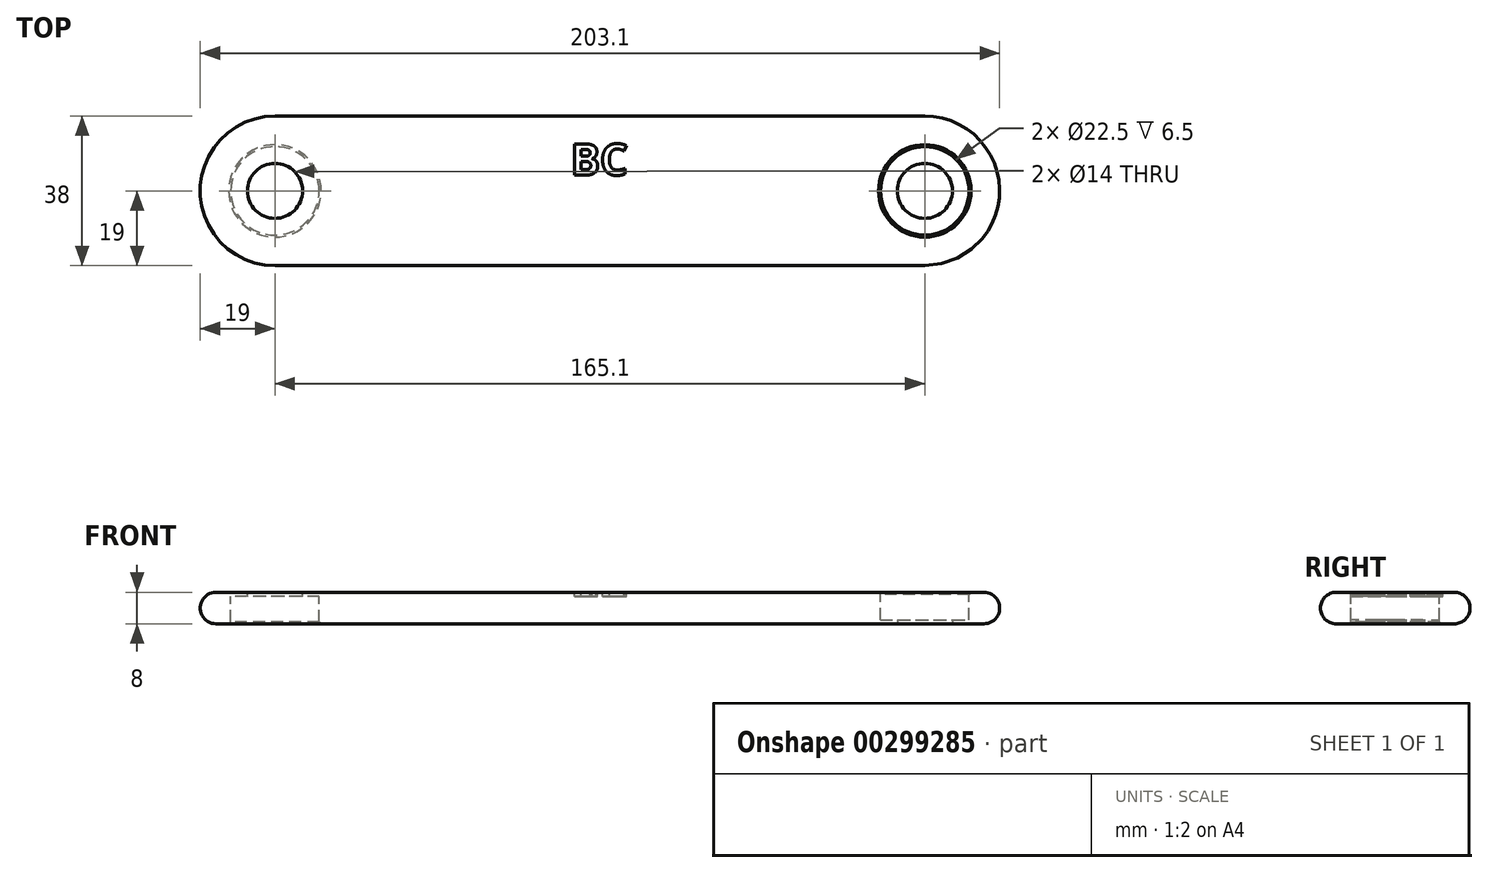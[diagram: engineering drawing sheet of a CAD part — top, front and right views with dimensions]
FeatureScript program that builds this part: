
annotation { "Feature Type Name" : "Feature", "Feature Type Description" : "" }
export const myFeature = defineFeature(function(context is Context, id is Id, definition is map)
    precondition{}
    {
        {
            var Q0;
            Q0=qCreatedBy(makeId("Top.planeOp"),FACE);
            var sketch = newSketch(context, id + "F0", { "sketchPlane" : qUnion([Q0])});
            skArc(sketch, "E0", {"start": v(-82.55, 19) * mm, "mid": v(-101.55, 0) * mm, "end": v(-82.55, -19) * mm});
            skArc(sketch, "E1", {"start": v(82.55, -19) * mm, "mid": v(101.55, 0) * mm, "end": v(82.55, 19) * mm});
            skCircle(sketch, "E2", {"center": v(-82.55, 0) * mm, "radius": 11.25 * mm});
            skCircle(sketch, "E3", {"center": v(82.55, 0) * mm, "radius": 11.25 * mm});
            skLineSegment(sketch, "E4", {"start": v(-82.55, 19) * mm, "end": v(82.55, 19) * mm});
            skLineSegment(sketch, "E5", {"start": v(-82.55, -19) * mm, "end": v(82.55, -19) * mm});
            skSolve(sketch);
        }
        {
            var Q0;
            Q0=makeQuery(id+"F0.imprint","IMPRINT",FACE,{"disambiguationData":[TD([[makeQuery(id+"F0.imprint","IMPRINT",EDGE,{"derivedFrom":sQuery(id+"F0.wireOp",EDGE,"E0")}),1.0]])]});
            extrude(context, id + "F1", {"entities" : qUnion([Q0]), "oppositeDirection" : true, "depth" : 8 * mm});
        }
        {
            var Q0;
            Q0=makeQuery(id+"F1.opExtrude","CAP_FACE",FACE,{"disambiguationData":[OSD([sQuery(id+"F0.wireOp",EDGE,"E0"),sQuery(id+"F0.wireOp",EDGE,"E1"),sQuery(id+"F0.wireOp",EDGE,"E2"),sQuery(id+"F0.wireOp",EDGE,"E3"),sQuery(id+"F0.wireOp",EDGE,"E4"),sQuery(id+"F0.wireOp",EDGE,"E5")])],"isStart":false});
            var sketch = newSketch(context, id + "F2", { "sketchPlane" : qUnion([Q0])});
            skCircle(sketch, "E6", {"center": v(82.55, 0) * mm, "radius": 7 * mm});
            skSolve(sketch);
        }
        {
            var Q0;
            Q0=makeQuery(id+"F2.imprint","IMPRINT",FACE,{"disambiguationData":[TD([[makeQuery(id+"F2.imprint","IMPRINT",EDGE,{"derivedFrom":sQuery(id+"F2.wireOp",EDGE,"E6")}),-1.0]])]});
            extrude(context, id + "F3", {"entities" : qUnion([Q0]), "operationType" : NewBodyOperationType.ADD, "oppositeDirection" : true, "depth" : 1 * mm});
        }
        {
            var Q0;
            Q0=makeQuery(id+"F0.imprint","IMPRINT",FACE,{"disambiguationData":[TD([[makeQuery(id+"F0.imprint","IMPRINT",EDGE,{"derivedFrom":sQuery(id+"F0.wireOp",EDGE,"E0")}),1.0]])]});
            var sketch = newSketch(context, id + "F4", { "sketchPlane" : qUnion([Q0])});
            skPoint(sketch, "E7.0", {"position": v(-82.55, 0) * mm});
            skCircle(sketch, "E8", {"center": v(-82.55, 0) * mm, "radius": 7 * mm});
            skCircle(sketch, "E9.0", {"center": v(-82.55, 0) * mm, "radius": 11.25 * mm});
            skSolve(sketch);
        }
        {
            var Q0;
            Q0=makeQuery(id+"F4.imprint","IMPRINT",FACE,{"disambiguationData":[TD([[makeQuery(id+"F4.imprint","IMPRINT",EDGE,{"derivedFrom":sQuery(id+"F4.wireOp",EDGE,"E8")}),-1.0]])]});
            extrude(context, id + "F5", {"entities" : qUnion([Q0]), "operationType" : NewBodyOperationType.ADD, "oppositeDirection" : true, "depth" : 1 * mm});
        }
        {
            var Q0;
            Q0=makeQuery(id+"F1.opExtrude","CAP_EDGE",EDGE,{"disambiguationData":[OSD([sQuery(id+"F0.wireOp",EDGE,"E5")])],"isStart":true});
            var Q1;
            Q1=makeQuery(id+"F1.opExtrude","CAP_EDGE",EDGE,{"disambiguationData":[OSD([sQuery(id+"F0.wireOp",EDGE,"E5")])],"isStart":false});
            fillet(context, id + "F6", {"entities" : qUnion([Q0, Q1]), "radius" : 4 * mm, "tangentPropagation" : true, "allowEdgeOverflow" : false});
        }
        {
            var Q0;
            Q0=makeQuery(id+"F5.boolean.opBoolean","MERGE",FACE,{"derivedFrom":[makeQuery(id+"F1.opExtrude","CAP_FACE",FACE,{"disambiguationData":[OSD([sQuery(id+"F0.wireOp",EDGE,"E0"),sQuery(id+"F0.wireOp",EDGE,"E1"),sQuery(id+"F0.wireOp",EDGE,"E2"),sQuery(id+"F0.wireOp",EDGE,"E3"),sQuery(id+"F0.wireOp",EDGE,"E4"),sQuery(id+"F0.wireOp",EDGE,"E5")])],"isStart":true}),makeQuery(id+"F5.opExtrude","CAP_FACE",FACE,{"disambiguationData":[OSD([sQuery(id+"F4.wireOp",EDGE,"E8"),sQuery(id+"F4.wireOp",EDGE,"E9.0")])],"isStart":true})]});
            var sketch = newSketch(context, id + "F7", { "sketchPlane" : qUnion([Q0])});
            skText(sketch, "E10", { "text": "BC", "fontName": "OpenSans-Bold.ttf"});
            const initialGuessF7  = {"E10": [-0.00744, 0.004, 1, 0, 0.008]};
            skSetInitialGuess(sketch, initialGuessF7);
            skSolve(sketch);
        }
        {
            var Q0;
            Q0 = qSketchRegion(id + "F7", true);
            extrude(context, id + "F8", {"entities" : qUnion([Q0]), "operationType" : NewBodyOperationType.REMOVE, "oppositeDirection" : true, "depth" : 1 * mm});
        }
        {
            var Q0;
            Q0=makeQuery(id+"F1.opExtrude","CAP_EDGE",EDGE,{"disambiguationData":[OSD([sQuery(id+"F0.wireOp",EDGE,"E3")])],"isStart":true});
            var Q1;
            Q1=makeQuery(id+"F1.opExtrude","CAP_EDGE",EDGE,{"disambiguationData":[OSD([sQuery(id+"F0.wireOp",EDGE,"E2")])],"isStart":false});
            chamfer(context, id + "F9", {"entities" : qUnion([Q0, Q1]), "width" : .5 * mm, "tangentPropagation" : true});
        }
    });
